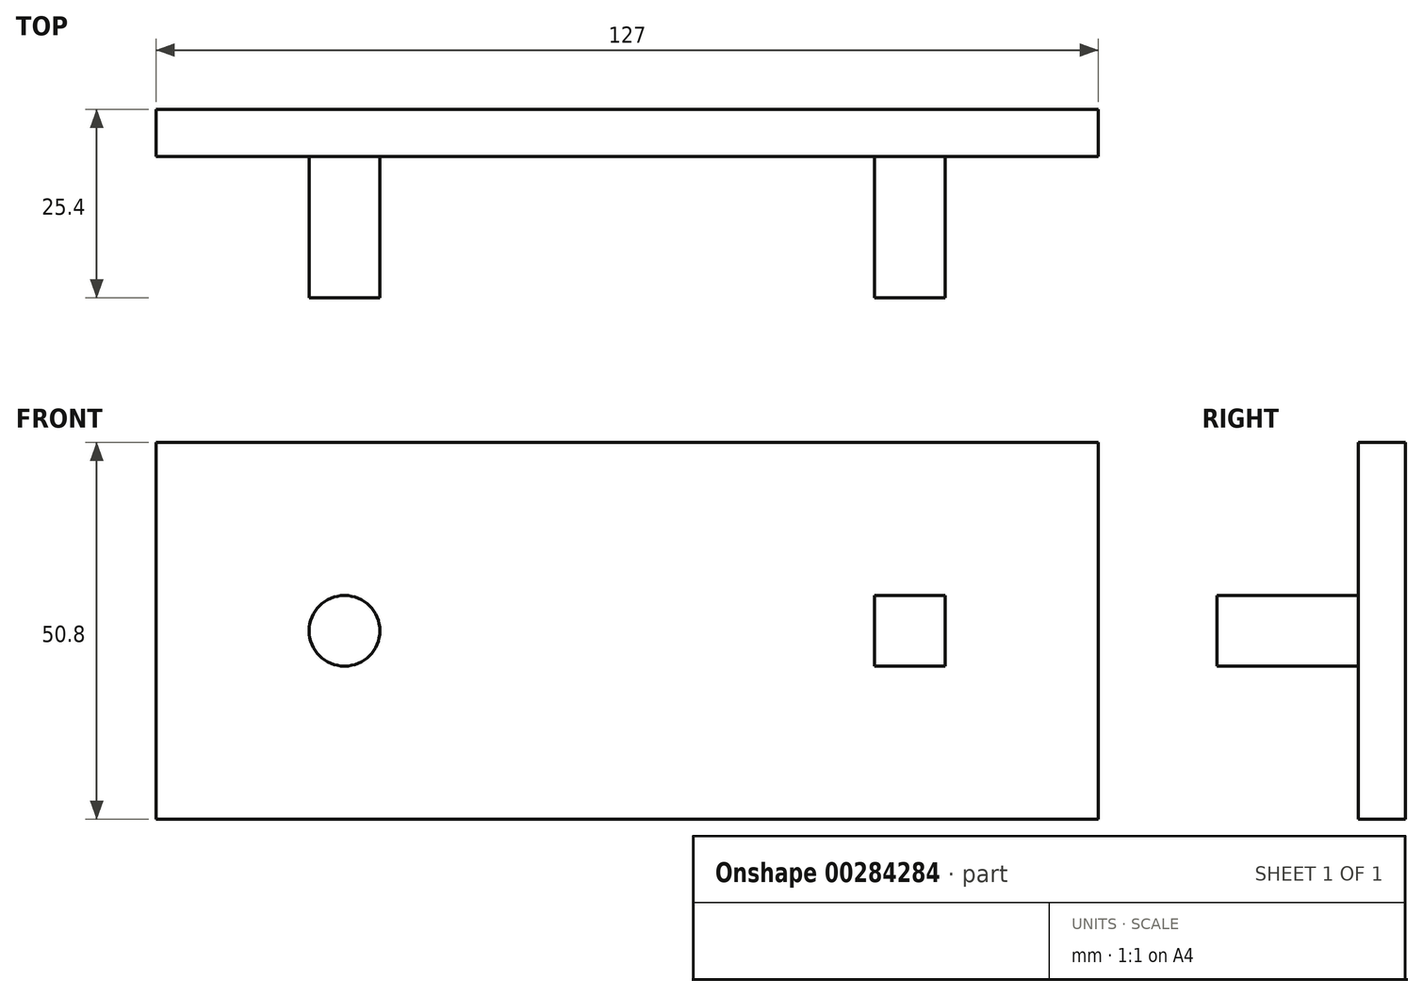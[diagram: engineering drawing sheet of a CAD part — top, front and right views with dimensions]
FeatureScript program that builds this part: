
annotation { "Feature Type Name" : "Feature", "Feature Type Description" : "" }
export const myFeature = defineFeature(function(context is Context, id is Id, definition is map)
    precondition{}
    {
        {
            var Q0;
            Q0=qCreatedBy(makeId("Front.planeOp"),FACE);
            var sketch = newSketch(context, id + "F0", { "sketchPlane" : qUnion([Q0])});
            skLineSegment(sketch, "E0.bottom", {"start": v(-85.41, 21.07) * mm, "end": v(41.59, 21.07) * mm});
            skLineSegment(sketch, "E0.top", {"start": v(-85.41, -29.73) * mm, "end": v(41.59, -29.73) * mm});
            skLineSegment(sketch, "E0.left", {"start": v(-85.41, 21.07) * mm, "end": v(-85.41, -29.73) * mm});
            skLineSegment(sketch, "E0.right", {"start": v(41.59, 21.07) * mm, "end": v(41.59, -29.73) * mm});
            skSolve(sketch);
        }
        {
            var Q0;
            Q0=makeQuery(id+"F0.imprint","IMPRINT",FACE,{"disambiguationData":[TD([[makeQuery(id+"F0.imprint","IMPRINT",EDGE,{"derivedFrom":sQuery(id+"F0.wireOp",EDGE,"E0.bottom")}),-1.0]])]});
            extrude(context, id + "F1", {"entities" : qUnion([Q0]), "depth" : 6.35 * mm});
        }
        {
            var Q0;
            Q0=makeQuery(id+"F1.opExtrude","CAP_FACE",FACE,{"disambiguationData":[OSD([sQuery(id+"F0.wireOp",EDGE,"E0.bottom"),sQuery(id+"F0.wireOp",EDGE,"E0.top"),sQuery(id+"F0.wireOp",EDGE,"E0.left"),sQuery(id+"F0.wireOp",EDGE,"E0.right")])],"isStart":false});
            var sketch = newSketch(context, id + "F2", { "sketchPlane" : qUnion([Q0])});
            skCircle(sketch, "E1", {"center": v(-60.01, -4.33) * mm, "radius": 4.76 * mm});
            skLineSegment(sketch, "E2.bottom", {"start": v(20.95, -9.1) * mm, "end": v(11.42, -9.1) * mm});
            skLineSegment(sketch, "E2.top", {"start": v(20.95, 0.43) * mm, "end": v(11.42, 0.43) * mm});
            skLineSegment(sketch, "E2.left", {"start": v(20.95, -9.1) * mm, "end": v(20.95, 0.43) * mm});
            skLineSegment(sketch, "E2.right", {"start": v(11.42, -9.1) * mm, "end": v(11.42, 0.43) * mm});
            skPoint(sketch, "E2.middle", {"position": v(16.19, -4.33) * mm});
            skPoint(sketch, "E3.orphan", {"position": v(41.59, -4.33) * mm});
            skPoint(sketch, "E4.orphan", {"position": v(16.19, 21.07) * mm});
            skPoint(sketch, "E5.orphan", {"position": v(16.19, -29.73) * mm});
            skPoint(sketch, "E6.orphan", {"position": v(-60.01, -29.73) * mm});
            skPoint(sketch, "E7.orphan", {"position": v(-85.41, -4.33) * mm});
            skPoint(sketch, "E8.orphan", {"position": v(-60.01, 21.07) * mm});
            skSolve(sketch);
        }
        {
            var Q0;
            Q0 = qSketchRegion(id + "F2", true);
            extrude(context, id + "F3", {"entities" : qUnion([Q0]), "operationType" : NewBodyOperationType.ADD, "depth" : 19.05 * mm});
        }
    });
